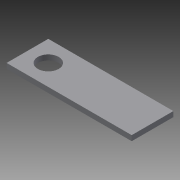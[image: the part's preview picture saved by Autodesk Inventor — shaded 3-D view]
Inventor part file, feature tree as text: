
AUTODESK INVENTOR PART (.ipt)
format: ipt  version: 2013 (Build 170138000, 138)  size: 101,888 bytes
history: native  units: in
note: dims shown in document units (in); Inventor stores cm internally (conversion verified against a paired STEP export)
features: extrude x5, sketch x5
ambient origin geometry x8: Origin, YZ Plane, XZ Plane, XY Plane, X Axis, Y Axis, Z Axis, Center Point
bodies: Solid1 (feature_tree)
feature tree (10):
  extrude  "Extrusion1"  Depth=1.0in
  extrude  "Extrusion2"  TaperAngle=0.0deg  [1 undecoded]
  extrude  "Extrusion3"  TaperAngle=180.0deg  [1 undecoded]
  extrude  "Extrusion4"  Depth=0.25in
  extrude  "Extrusion5"  Depth=0.125in TaperAngle=0.0deg
  sketch  "Sketch1"  dims[d0=6.0in d1=1.0in]
  sketch  "Sketch2"  dims[d2=0.5in d3=0.0in]
  sketch  "Sketch3"  dims[d4=1.0in d5=180.0deg]
  sketch  "Sketch4"  dims[d6=1.0in d7=0.25in]
  sketch  "Sketch5"  dims[d8=0.25in d9=0.125in d10=0.0in d11=0.25in d12=1.0in d13=0.0in d14=0.5in d15=1.0in d16=0.0in d17=1.0in d18=0.0in d19=0.125in d20=0.0in]
note: 2 required parameter values undecoded (feature->parameter linkage not recoverable at this tier; creation-order binding heuristic only, values carry confidence <= 0.55)
